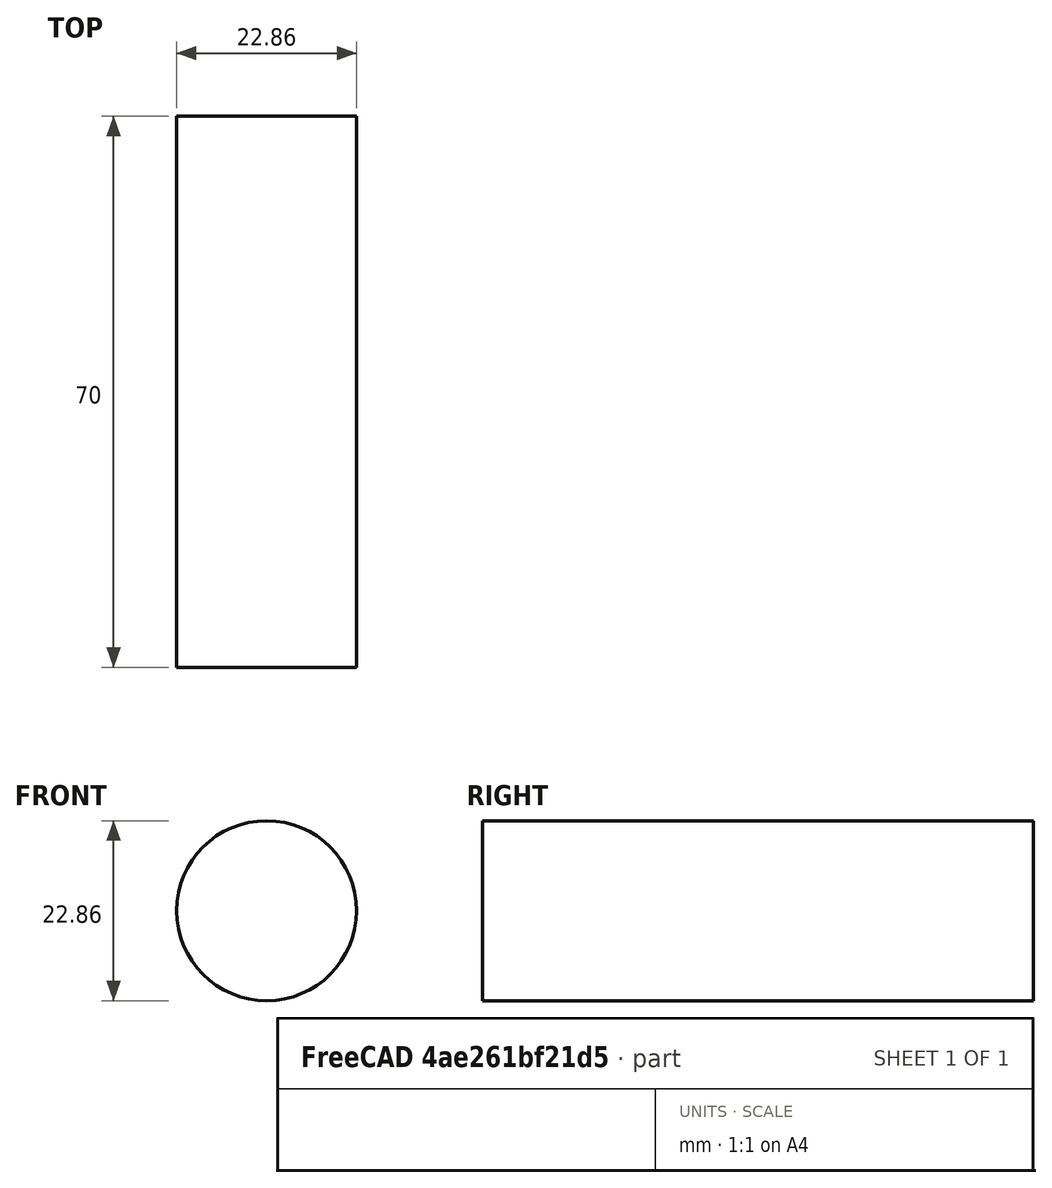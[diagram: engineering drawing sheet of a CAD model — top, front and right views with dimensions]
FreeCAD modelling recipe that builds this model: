
FCSTD DOCUMENT  (FreeCAD 1.1R20260325 (Git shallow))
Label: battery
License: All rights reserved
LicenseURL: https://en.wikipedia.org/wiki/All_rights_reserved
objects: Mesh::Feature×1, App::Point×1, Sketcher::SketchObject×1, PartDesign::Pad×1, PartDesign::Body×1
note: 6 computed .brp shape members not serialized (recipe doc carries the construction recipe); baked Part::Feature solids carry a one-line shape summary decoded from their .brp

FEATURE [Mesh::Feature] coin
FEATURE [App::Point] Origin001
  Role = Origin
FEATURE [Sketcher::SketchObject] Sketch
  ArcFitTolerance = 1e-06
  AttachmentSupport = -> [Origin]
  ExternalTypes = [0]
  FullyConstrained = false
  MakeInternals = true
  MapMode = 5
  Placement = pos=(0,0,0) rot=(1,0,0;1.5708rad)
  _ExternalGeoVersion = 1
  sketch-geometry (1):
    g0: Circle CenterX=0.121635 CenterY=0 CenterZ=0 NormalX=0 NormalY=0 NormalZ=1 AngleXU=0 Radius=11.43
  constraints (2):
    c: Diameter(g0) = 22.86
    c: PointOnObject(g0,g-1)
FEATURE [PartDesign::Pad] Pad
  Direction = (0,-1,0)
  Length = 70
  Length2 = 10
  Profile = -> Sketch
  ReferenceAxis = -> Sketch [N_Axis]
  Refine = true
  SideType = 0
  Suppressed = false
  Type = 0
  Type2 = 0
FEATURE [PartDesign::Body] Body
  AllowCompound = false
  Group = -> [Sketch,Pad]
  Origin = -> Origin
  Tip = -> Pad
